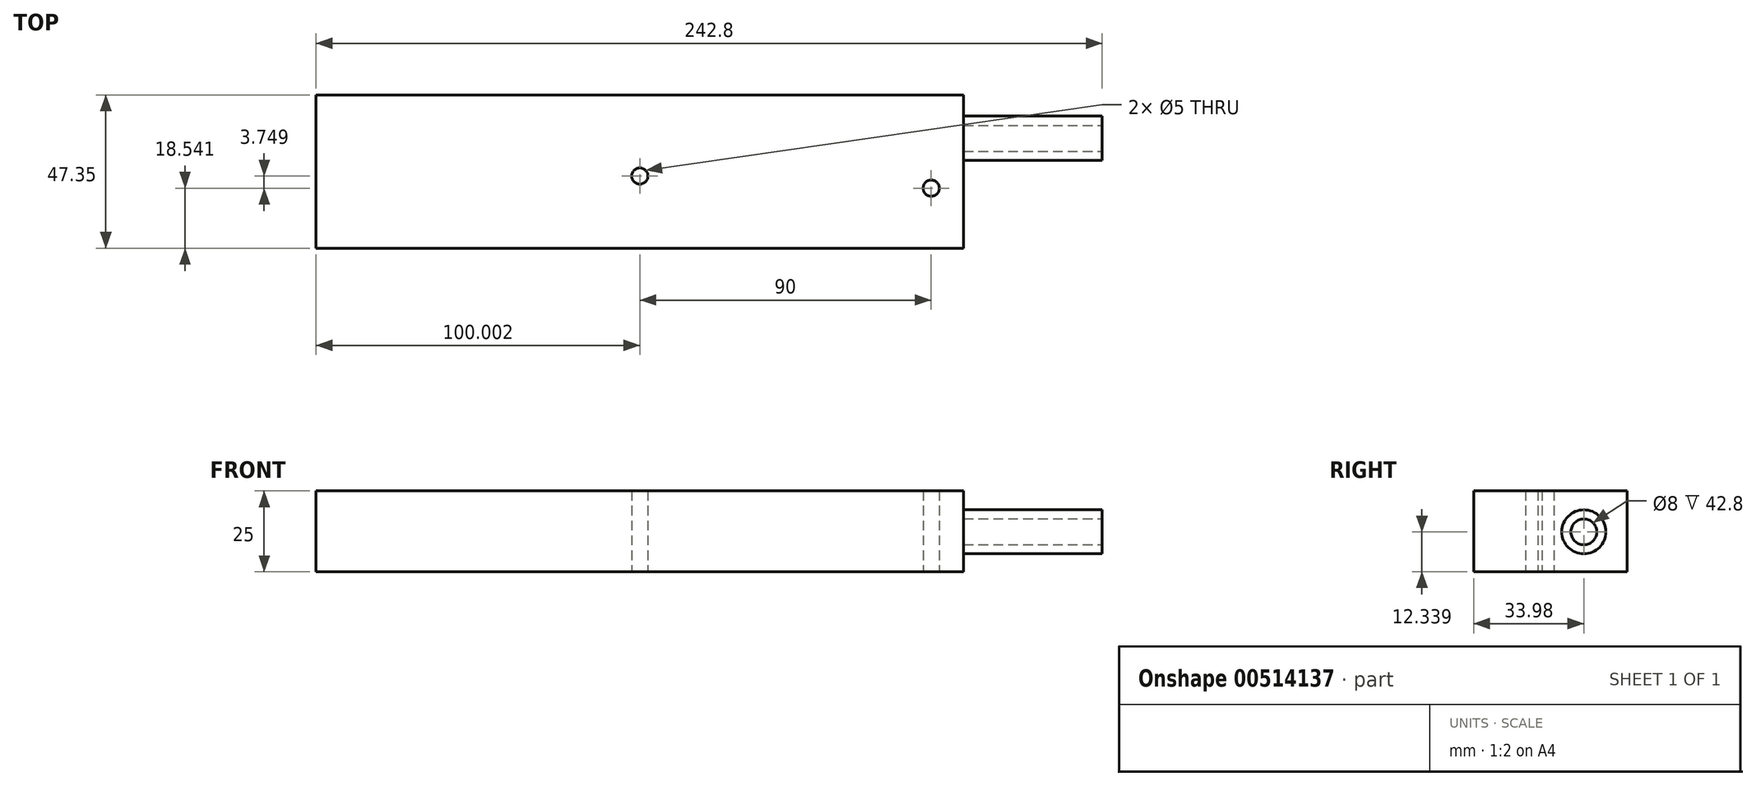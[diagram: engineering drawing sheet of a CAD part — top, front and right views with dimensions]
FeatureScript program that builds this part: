
annotation { "Feature Type Name" : "Feature", "Feature Type Description" : "" }
export const myFeature = defineFeature(function(context is Context, id is Id, definition is map)
    precondition{}
    {
        {
            var Q0;
            Q0=qCreatedBy(makeId("Top.planeOp"),FACE);
            var sketch = newSketch(context, id + "F0", { "sketchPlane" : qUnion([Q0])});
            skLineSegment(sketch, "E0.bottom", {"start": v(-21.2, 13.37) * mm, "end": v(178.8, 13.37) * mm});
            skLineSegment(sketch, "E0.top", {"start": v(-21.2, -33.98) * mm, "end": v(178.8, -33.98) * mm});
            skLineSegment(sketch, "E0.left", {"start": v(-21.2, 13.37) * mm, "end": v(-21.2, -33.98) * mm});
            skLineSegment(sketch, "E0.right", {"start": v(178.8, 13.37) * mm, "end": v(178.8, -33.98) * mm});
            skCircle(sketch, "E1", {"center": v(78.8, -11.69) * mm, "radius": 2.5 * mm});
            skCircle(sketch, "E2", {"center": v(168.8, -15.44) * mm, "radius": 2.5 * mm});
            skLineSegment(sketch, "E3", {"start": v(78.8, 13.37) * mm, "end": v(78.8, -33.98) * mm, "construction": true});
            skLineSegment(sketch, "E4", {"start": v(-21.2, -10.3) * mm, "end": v(178.8, -13.08) * mm, "construction": true});
            skCircle(sketch, "E5", {"center": v(78.8, -11.69) * mm, "radius": 7.24 * mm, "construction": true});
            skSolve(sketch);
        }
        {
            var Q0;
            Q0 = qSketchRegion(id + "F0", true);
            extrude(context, id + "F1", {"entities" : qUnion([Q0]), "depth" : 25 * mm});
        }
        {
            var Q0;
            Q0=makeQuery(id+"F1.opExtrude","SWEPT_FACE",FACE,{"disambiguationData":[OSD([sQuery(id+"F0.wireOp",EDGE,"E0.right")])]});
            var sketch = newSketch(context, id + "F2", { "sketchPlane" : qUnion([Q0])});
            skCircle(sketch, "E6", {"center": v(0, 12.34) * mm, "radius": 6.8 * mm});
            skSolve(sketch);
        }
        {
            var Q0;
            Q0 = qSketchRegion(id + "F2", true);
            extrude(context, id + "F3", {"entities" : qUnion([Q0]), "operationType" : NewBodyOperationType.ADD, "depth" : 42.8 * mm});
        }
        {
            var Q0;
            Q0=makeQuery(id+"F3.opExtrude","CAP_FACE",FACE,{"disambiguationData":[OSD([sQuery(id+"F2.wireOp",EDGE,"E6")])],"isStart":false});
            var sketch = newSketch(context, id + "F4", { "sketchPlane" : qUnion([Q0])});
            skCircle(sketch, "E7", {"center": v(0, 12.34) * mm, "radius": 4 * mm});
            skSolve(sketch);
        }
        {
            var Q0;
            Q0 = qSketchRegion(id + "F4", true);
            var Q1;
            Q1=makeQuery(id+"F1.opExtrude","SWEPT_FACE",FACE,{"disambiguationData":[OSD([sQuery(id+"F0.wireOp",EDGE,"E0.right")])]});
            extrude(context, id + "F5", {"entities" : qUnion([Q0]), "operationType" : NewBodyOperationType.REMOVE, "endBound" : BoundingType.UP_TO_SURFACE, "oppositeDirection" : true, "endBoundEntityFace" : qUnion([Q1]), "depth" : 25 * mm});
        }
    });
